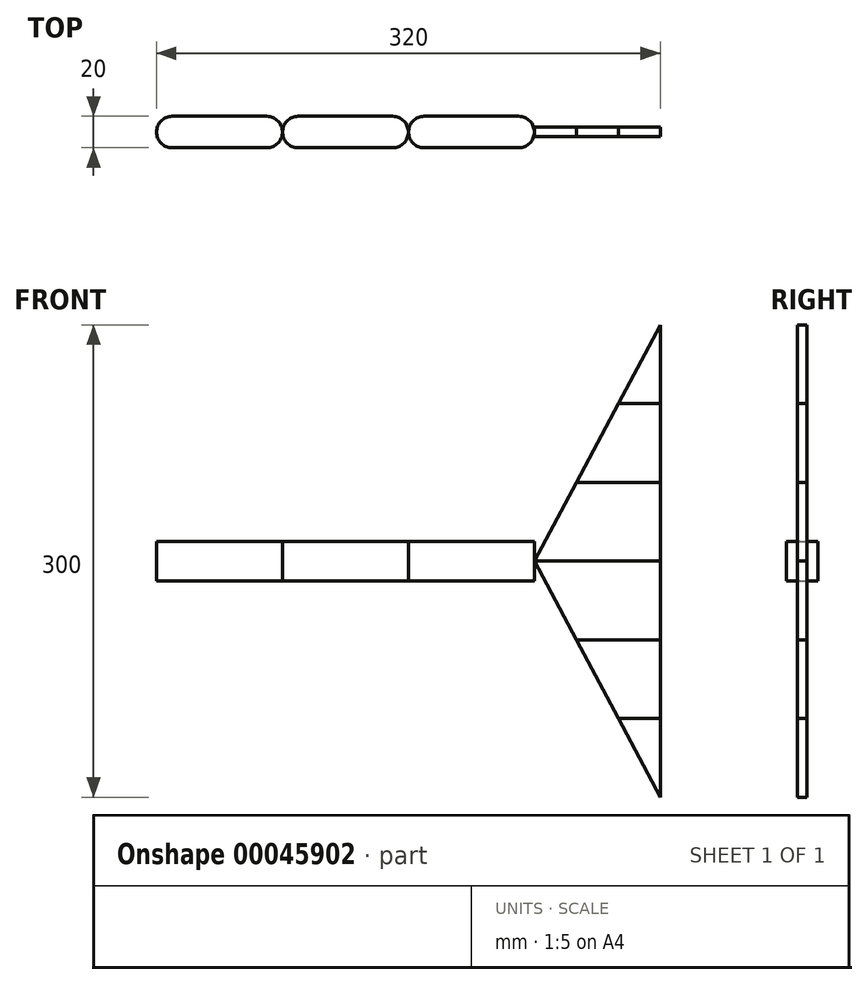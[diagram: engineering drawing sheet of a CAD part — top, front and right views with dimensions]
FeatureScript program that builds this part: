
annotation { "Feature Type Name" : "Feature", "Feature Type Description" : "" }
export const myFeature = defineFeature(function(context is Context, id is Id, definition is map)
    precondition{}
    {
        {
            var Q0;
            Q0=qCreatedBy(makeId("Top.planeOp"),FACE);
            var sketch = newSketch(context, id + "F0", { "sketchPlane" : qUnion([Q0])});
            skCircle(sketch, "E0", {"center": v(0, 0) * mm, "radius": 10 * mm});
            skLineSegment(sketch, "E1.bottom", {"start": v(0, 10) * mm, "end": v(60, 10) * mm});
            skLineSegment(sketch, "E1.top", {"start": v(0, -10) * mm, "end": v(60, -10) * mm});
            skLineSegment(sketch, "E1.left", {"start": v(0, 10) * mm, "end": v(0, -10) * mm});
            skLineSegment(sketch, "E1.right", {"start": v(60, 10) * mm, "end": v(60, -10) * mm});
            skCircle(sketch, "E2", {"center": v(60, 0) * mm, "radius": 10 * mm});
            skSolve(sketch);
        }
        {
            var Q0;
            {var subQ0=sQuery(id+"F0.wireOp",EDGE,"E1.left");Q0=makeQuery(id+"F0.imprint","IMPRINT",FACE,{"disambiguationData":[TD([[makeQuery(id+"F0.imprint","IMPRINT",EDGE,{"derivedFrom":subQ0}),-1.0]])]});}
            var Q1;
            {var subQ0=sQuery(id+"F0.wireOp",EDGE,"E1.left");Q1=makeQuery(id+"F0.imprint","IMPRINT",FACE,{"disambiguationData":[TD([[makeQuery(id+"F0.imprint","IMPRINT",EDGE,{"derivedFrom":subQ0}),1.0]])]});}
            var Q2;
            {var subQ3=sQuery(id+"F0.wireOp",EDGE,"E1.bottom");Q2=makeQuery(id+"F0.imprint","IMPRINT",FACE,{"disambiguationData":[TD([[makeQuery(id+"F0.imprint","IMPRINT",EDGE,{"derivedFrom":subQ3}),-1.0]])]});}
            var Q3;
            {var subQ1=sQuery(id+"F0.wireOp",EDGE,"E1.right");Q3=makeQuery(id+"F0.imprint","IMPRINT",FACE,{"disambiguationData":[TD([[makeQuery(id+"F0.imprint","IMPRINT",EDGE,{"derivedFrom":subQ1}),-1.0]])]});}
            var Q4;
            {var subQ1=sQuery(id+"F0.wireOp",EDGE,"E1.right");Q4=makeQuery(id+"F0.imprint","IMPRINT",FACE,{"disambiguationData":[TD([[makeQuery(id+"F0.imprint","IMPRINT",EDGE,{"derivedFrom":subQ1}),1.0]])]});}
            extrude(context, id + "F1", {"entities" : qUnion([Q0, Q1, Q2, Q3, Q4]), "endBound" : BoundingType.SYMMETRIC, "depth" : 25 * mm});
        }
        {
            var Q0;
            Q0=makeQuery(id+"F1.opExtrude","SWEPT_BODY",BODY,{"disambiguationData":[OSD([sQuery(id+"F0.wireOp",EDGE,"E0"),sQuery(id+"F0.wireOp",EDGE,"E1.bottom"),sQuery(id+"F0.wireOp",EDGE,"E1.top"),sQuery(id+"F0.wireOp",EDGE,"E2")])]});
            transform(context, id + "F2", {"entities" : qUnion([Q0]), "transformType" : TransformType.TRANSLATION_3D, "dx" : 80 * mm, "dy" : 0 * mm, "dz" : 0 * mm, "makeCopy" : true});
        }
        {
            var Q0;
            Q0=makeQuery(id+"F2.opPattern","COPY",BODY,{"derivedFrom":makeQuery(id+"F1.opExtrude","SWEPT_BODY",BODY,{"disambiguationData":[OSD([sQuery(id+"F0.wireOp",EDGE,"E0"),sQuery(id+"F0.wireOp",EDGE,"E1.bottom"),sQuery(id+"F0.wireOp",EDGE,"E1.top"),sQuery(id+"F0.wireOp",EDGE,"E2")])]}),"instanceName":"1"});
            transform(context, id + "F3", {"entities" : qUnion([Q0]), "transformType" : TransformType.TRANSLATION_3D, "dx" : 80 * mm, "dy" : 0 * mm, "dz" : 0 * mm, "makeCopy" : true});
        }
        {
            var Q0;
            Q0=qCreatedBy(makeId("Front.planeOp"),FACE);
            var sketch = newSketch(context, id + "F4", { "sketchPlane" : qUnion([Q0])});
            skLineSegment(sketch, "E3", {"start": v(230, 0) * mm, "end": v(310, 150) * mm});
            skLineSegment(sketch, "E4", {"start": v(310, 150) * mm, "end": v(310, 0) * mm});
            skLineSegment(sketch, "E5", {"start": v(310, 0) * mm, "end": v(230, 0) * mm});
            skLineSegment(sketch, "E6", {"start": v(256.67, 50) * mm, "end": v(310, 50) * mm});
            skLineSegment(sketch, "E7", {"start": v(283.33, 100) * mm, "end": v(310, 100) * mm});
            skSolve(sketch);
        }
        {
            var Q0;
            {var subQ1=sQuery(id+"F4.wireOp",EDGE,"E5");Q0=makeQuery(id+"F4.imprint","IMPRINT",FACE,{"disambiguationData":[TD([[makeQuery(id+"F4.imprint","IMPRINT",EDGE,{"derivedFrom":subQ1}),-1.0]])]});}
            extrude(context, id + "F5", {"entities" : qUnion([Q0]), "endBound" : BoundingType.SYMMETRIC, "depth" : 6 * mm});
        }
        {
            var Q0;
            {var subQ1=sQuery(id+"F4.wireOp",EDGE,"E6");Q0=makeQuery(id+"F4.imprint","IMPRINT",FACE,{"disambiguationData":[TD([[makeQuery(id+"F4.imprint","IMPRINT",EDGE,{"derivedFrom":subQ1}),1.0]])]});}
            extrude(context, id + "F6", {"entities" : qUnion([Q0]), "endBound" : BoundingType.SYMMETRIC, "depth" : 6 * mm});
        }
        {
            var Q0;
            {var subQ1=sQuery(id+"F4.wireOp",EDGE,"E7");Q0=makeQuery(id+"F4.imprint","IMPRINT",FACE,{"disambiguationData":[TD([[makeQuery(id+"F4.imprint","IMPRINT",EDGE,{"derivedFrom":subQ1}),1.0]])]});}
            extrude(context, id + "F7", {"entities" : qUnion([Q0]), "endBound" : BoundingType.SYMMETRIC, "depth" : 6 * mm});
        }
        {
            var Q0;
            Q0=makeQuery(id+"F5.opExtrude","SWEPT_BODY",BODY,{"disambiguationData":[OSD([sQuery(id+"F4.wireOp",EDGE,"E3"),sQuery(id+"F4.wireOp",EDGE,"E4"),sQuery(id+"F4.wireOp",EDGE,"E5"),sQuery(id+"F4.wireOp",EDGE,"E6")])]});
            var Q1;
            Q1=qCreatedBy(makeId("Top.planeOp"),FACE);
            mirror(context, id + "F8", {"entities" : qUnion([Q0]), "mirrorPlane" : qUnion([Q1])});
        }
        {
            var Q0;
            Q0=makeQuery(id+"F6.opExtrude","SWEPT_BODY",BODY,{"disambiguationData":[OSD([sQuery(id+"F4.wireOp",EDGE,"E3"),sQuery(id+"F4.wireOp",EDGE,"E4"),sQuery(id+"F4.wireOp",EDGE,"E6"),sQuery(id+"F4.wireOp",EDGE,"E7")])]});
            var Q1;
            Q1=qCreatedBy(makeId("Top.planeOp"),FACE);
            mirror(context, id + "F9", {"entities" : qUnion([Q0]), "mirrorPlane" : qUnion([Q1])});
        }
        {
            var Q0;
            Q0=makeQuery(id+"F7.opExtrude","SWEPT_BODY",BODY,{"disambiguationData":[OSD([sQuery(id+"F4.wireOp",EDGE,"E3"),sQuery(id+"F4.wireOp",EDGE,"E4"),sQuery(id+"F4.wireOp",EDGE,"E7")])]});
            var Q1;
            Q1=qCreatedBy(makeId("Top.planeOp"),FACE);
            mirror(context, id + "F10", {"entities" : qUnion([Q0]), "mirrorPlane" : qUnion([Q1])});
        }
    });
